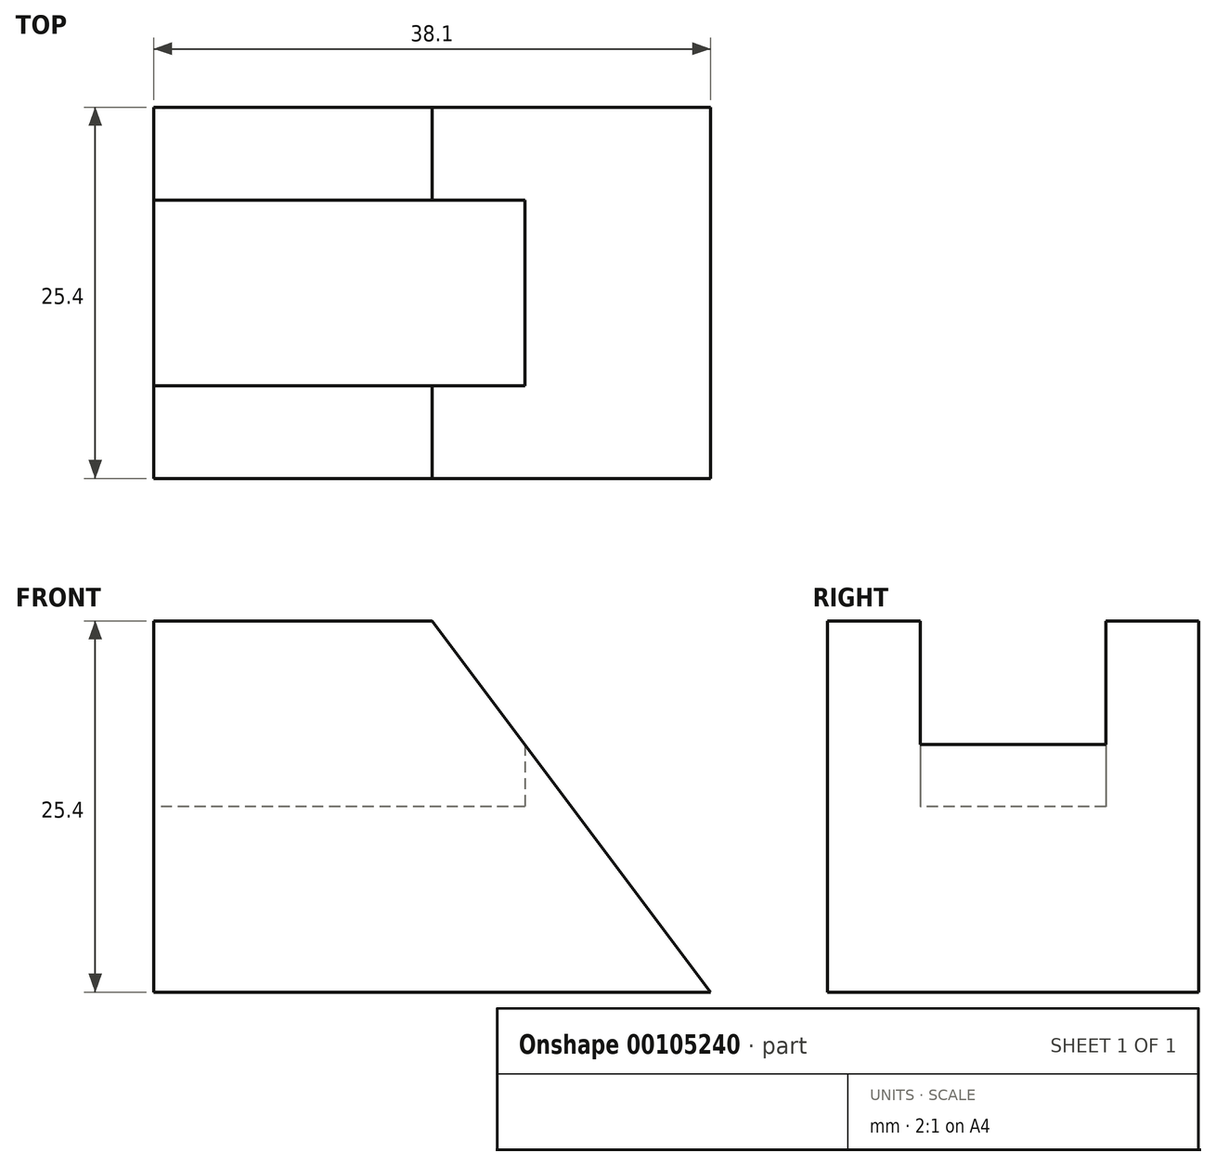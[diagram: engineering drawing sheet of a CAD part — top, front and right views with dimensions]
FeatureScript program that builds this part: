
annotation { "Feature Type Name" : "Feature", "Feature Type Description" : "" }
export const myFeature = defineFeature(function(context is Context, id is Id, definition is map)
    precondition{}
    {
        {
            var Q0;
            Q0=qCreatedBy(makeId("Front.planeOp"),FACE);
            var sketch = newSketch(context, id + "F0", { "sketchPlane" : qUnion([Q0])});
            skLineSegment(sketch, "E0.bottom", {"start": v(0, 0) * mm, "end": v(38.1, 0) * mm});
            skLineSegment(sketch, "E0.top", {"start": v(0, 25.4) * mm, "end": v(38.1, 25.4) * mm});
            skLineSegment(sketch, "E0.left", {"start": v(0, 0) * mm, "end": v(0, 25.4) * mm});
            skLineSegment(sketch, "E0.right", {"start": v(38.1, 0) * mm, "end": v(38.1, 25.4) * mm});
            skSolve(sketch);
        }
        {
            var Q0;
            Q0 = qSketchRegion(id + "F0", true);
            extrude(context, id + "F1", {"entities" : qUnion([Q0]), "endBound" : BoundingType.SYMMETRIC, "depth" : 25.4 * mm});
        }
        {
            var Q0;
            Q0=makeQuery(id+"F1.opExtrude","CAP_FACE",FACE,{"disambiguationData":[OSD([sQuery(id+"F0.wireOp",EDGE,"E0.bottom"),sQuery(id+"F0.wireOp",EDGE,"E0.top"),sQuery(id+"F0.wireOp",EDGE,"E0.left"),sQuery(id+"F0.wireOp",EDGE,"E0.right")])],"isStart":false});
            var sketch = newSketch(context, id + "F2", { "sketchPlane" : qUnion([Q0])});
            skLineSegment(sketch, "E1", {"start": v(19.05, 25.4) * mm, "end": v(38.1, 0) * mm});
            skSolve(sketch);
        }
        {
            var Q0;
            {var subQ0=sQuery(id+"F2.wireOp",EDGE,"E1");Q0=makeQuery(id+"F2.imprint","IMPRINT",FACE,{"disambiguationData":[TD([[makeQuery(id+"F2.imprint","IMPRINT",EDGE,{"derivedFrom":subQ0}),1.0]])]});}
            extrude(context, id + "F3", {"entities" : qUnion([Q0]), "operationType" : NewBodyOperationType.REMOVE, "oppositeDirection" : true, "depth" : 25.4 * mm});
        }
        {
            var Q0;
            Q0=qCreatedBy(makeId("Right.planeOp"),FACE);
            var sketch = newSketch(context, id + "F4", { "sketchPlane" : qUnion([Q0])});
            skLineSegment(sketch, "E2.bottom", {"start": v(6.35, 25.4) * mm, "end": v(-6.35, 25.4) * mm});
            skLineSegment(sketch, "E2.top", {"start": v(6.35, 12.7) * mm, "end": v(-6.35, 12.7) * mm});
            skLineSegment(sketch, "E2.left", {"start": v(6.35, 25.4) * mm, "end": v(6.35, 12.7) * mm});
            skLineSegment(sketch, "E2.right", {"start": v(-6.35, 25.4) * mm, "end": v(-6.35, 12.7) * mm});
            skSolve(sketch);
        }
        {
            var Q0;
            Q0=makeQuery(id+"F4.imprint","IMPRINT",FACE,{"disambiguationData":[TD([[makeQuery(id+"F4.imprint","IMPRINT",EDGE,{"derivedFrom":sQuery(id+"F4.wireOp",EDGE,"E2.bottom")}),1.0]])]});
            extrude(context, id + "F5", {"entities" : qUnion([Q0]), "operationType" : NewBodyOperationType.REMOVE, "depth" : 25.4 * mm});
        }
    });
